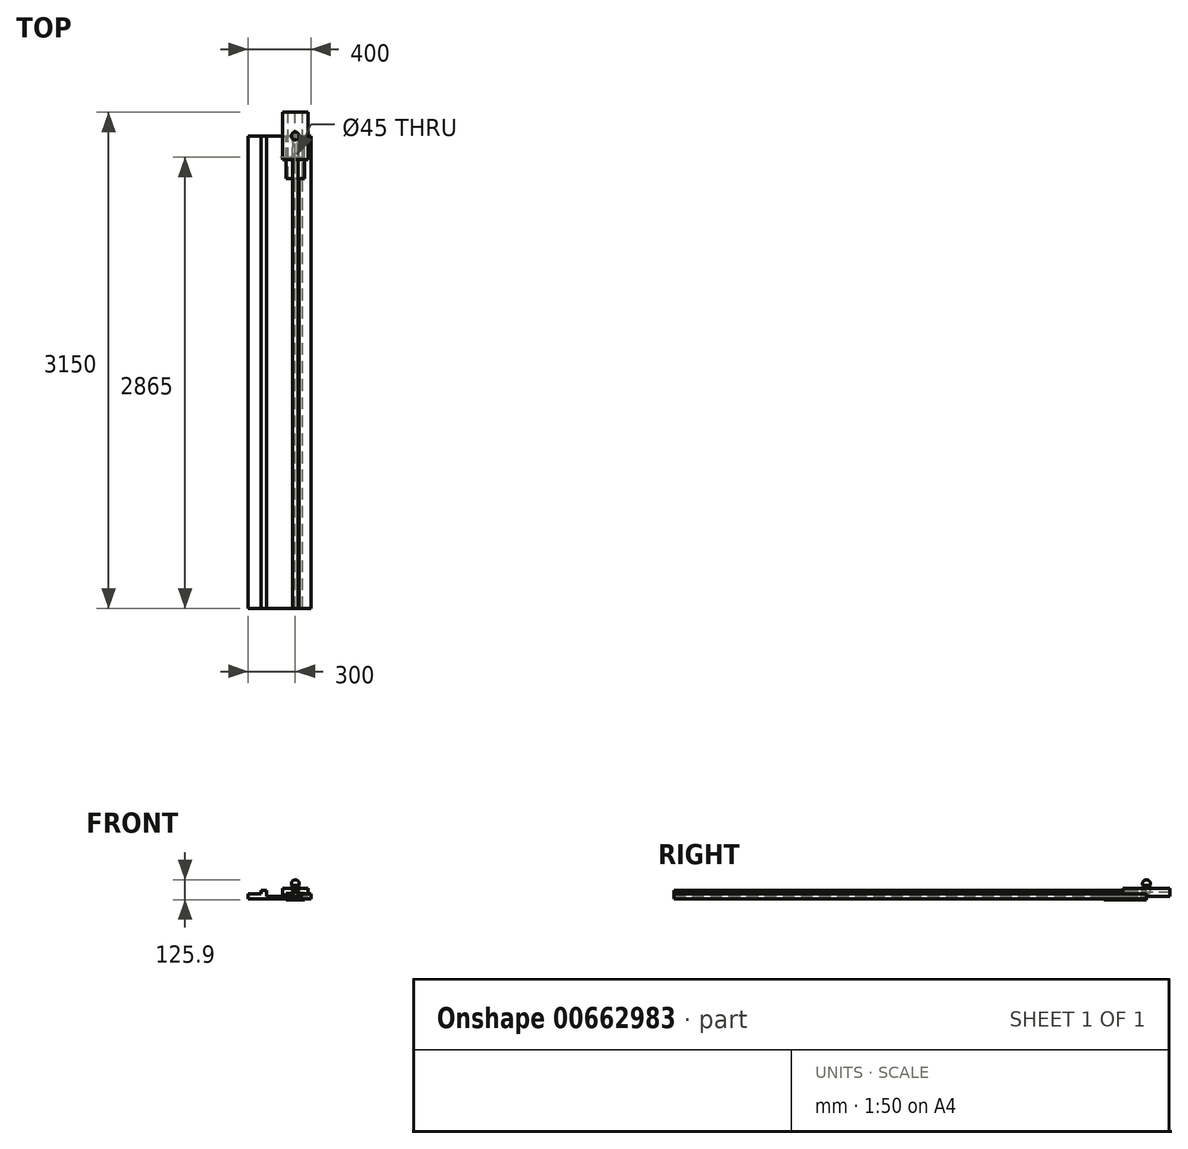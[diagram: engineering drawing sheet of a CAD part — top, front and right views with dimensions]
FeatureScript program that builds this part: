
annotation { "Feature Type Name" : "Feature", "Feature Type Description" : "" }
export const myFeature = defineFeature(function(context is Context, id is Id, definition is map)
    precondition{}
    {
        {
            var Q0;
            Q0=qCreatedBy(makeId("Front.planeOp"),FACE);
            var sketch = newSketch(context, id + "F0", { "sketchPlane" : qUnion([Q0])});
            skLineSegment(sketch, "E0.bottom", {"start": v(100, -15) * mm, "end": v(-100, -15) * mm});
            skLineSegment(sketch, "E0.top", {"start": v(100, 15) * mm, "end": v(-100, 15) * mm});
            skLineSegment(sketch, "E0.left", {"start": v(100, -15) * mm, "end": v(100, 15) * mm});
            skLineSegment(sketch, "E0.right", {"start": v(-100, -15) * mm, "end": v(-100, 15) * mm});
            skPoint(sketch, "E0.middle", {"position": v(0, 0) * mm});
            skLineSegment(sketch, "E1.bottom", {"start": v(-17.5, 15) * mm, "end": v(17.5, 15) * mm});
            skLineSegment(sketch, "E1.top", {"start": v(-17.5, 40) * mm, "end": v(17.5, 40) * mm});
            skLineSegment(sketch, "E1.left", {"start": v(-17.5, 15) * mm, "end": v(-17.5, 40) * mm});
            skLineSegment(sketch, "E1.right", {"start": v(17.5, 15) * mm, "end": v(17.5, 40) * mm});
            skPoint(sketch, "E1.middle", {"position": v(0, 27.5) * mm});
            skLineSegment(sketch, "E2.bottom", {"start": v(-100, 15) * mm, "end": v(-300, 15) * mm});
            skLineSegment(sketch, "E2.top", {"start": v(-100, -15) * mm, "end": v(-300, -15) * mm});
            skLineSegment(sketch, "E2.left", {"start": v(-100, 15) * mm, "end": v(-100, -15) * mm});
            skLineSegment(sketch, "E2.right", {"start": v(-300, 15) * mm, "end": v(-300, -15) * mm});
            skLineSegment(sketch, "E3.bottom", {"start": v(-182.5, 15) * mm, "end": v(-217.5, 15) * mm});
            skLineSegment(sketch, "E3.top", {"start": v(-182.5, 40) * mm, "end": v(-217.5, 40) * mm});
            skLineSegment(sketch, "E3.left", {"start": v(-182.5, 15) * mm, "end": v(-182.5, 40) * mm});
            skLineSegment(sketch, "E3.right", {"start": v(-217.5, 15) * mm, "end": v(-217.5, 40) * mm});
            skPoint(sketch, "E3.middle", {"position": v(-200, 27.5) * mm});
            skPoint(sketch, "E3.middle.positionSnap0", {"position": v(-200, 15) * mm});
            skPoint(sketch, "E3.centerSnap0", {"position": v(-200, 15) * mm});
            skSolve(sketch);
        }
        {
            var Q0;
            Q0=makeQuery(id+"F0.imprint","IMPRINT",FACE,{"disambiguationData":[TD([[makeQuery(id+"F0.imprint","IMPRINT",EDGE,{"derivedFrom":sQuery(id+"F0.wireOp",EDGE,"E1.top")}),-1.0]])]});
            var Q1;
            Q1=makeQuery(id+"F0.imprint","IMPRINT",FACE,{"disambiguationData":[TD([[makeQuery(id+"F0.imprint","IMPRINT",EDGE,{"derivedFrom":sQuery(id+"F0.wireOp",EDGE,"E0.bottom")}),-1.0]])]});
            var Q2;
            Q2=makeQuery(id+"F0.imprint","IMPRINT",FACE,{"disambiguationData":[TD([[makeQuery(id+"F0.imprint","IMPRINT",EDGE,{"derivedFrom":sQuery(id+"F0.wireOp",EDGE,"E3.top")}),1.0]])]});
            var Q3;
            {var subQ3=sQuery(id+"F0.wireOp",EDGE,"E0.right");Q3=makeQuery(id+"F0.imprint","IMPRINT",FACE,{"disambiguationData":[TD([[makeQuery(id+"F0.imprint","IMPRINT",EDGE,{"derivedFrom":subQ3}),1.0]])]});}
            extrude(context, id + "F1", {"entities" : qUnion([Q0, Q1, Q2, Q3]), "depth" : 3000 * mm, "offsetDistance" : 25 * mm});
        }
        {
            var Q0;
            Q0=makeQuery(id+"F1.opExtrude","CAP_FACE",FACE,{"disambiguationData":[OSD([sQuery(id+"F0.wireOp",EDGE,"E0.bottom"),sQuery(id+"F0.wireOp",EDGE,"E0.top"),sQuery(id+"F0.wireOp",EDGE,"E0.left"),sQuery(id+"F0.wireOp",EDGE,"E1.top"),sQuery(id+"F0.wireOp",EDGE,"E1.left"),sQuery(id+"F0.wireOp",EDGE,"E1.right"),sQuery(id+"F0.wireOp",EDGE,"E2.bottom"),sQuery(id+"F0.wireOp",EDGE,"E2.top"),sQuery(id+"F0.wireOp",EDGE,"E2.right"),sQuery(id+"F0.wireOp",EDGE,"E3.top"),sQuery(id+"F0.wireOp",EDGE,"E3.left"),sQuery(id+"F0.wireOp",EDGE,"E3.right")])],"isStart":false});
            var sketch = newSketch(context, id + "F2", { "sketchPlane" : qUnion([Q0])});
            skLineSegment(sketch, "E4.bottom", {"start": v(-182.5, 15) * mm, "end": v(-17.5, 15) * mm});
            skLineSegment(sketch, "E4.top", {"start": v(-182.5, 0) * mm, "end": v(-17.5, 0) * mm});
            skLineSegment(sketch, "E4.left", {"start": v(-182.5, 15) * mm, "end": v(-182.5, 0) * mm});
            skLineSegment(sketch, "E4.right", {"start": v(-17.5, 15) * mm, "end": v(-17.5, 0) * mm});
            skSolve(sketch);
        }
        {
            var Q0;
            Q0=makeQuery(id+"F2.imprint","IMPRINT",FACE,{"disambiguationData":[TD([[makeQuery(id+"F2.imprint","IMPRINT",EDGE,{"derivedFrom":sQuery(id+"F2.wireOp",EDGE,"E4.bottom")}),1.0]])]});
            extrude(context, id + "F3", {"entities" : qUnion([Q0]), "operationType" : NewBodyOperationType.REMOVE, "endBound" : BoundingType.THROUGH_ALL, "oppositeDirection" : true, "depth" : 25 * mm, "offsetDistance" : 25 * mm});
        }
        {
            var Q0;
            Q0=qCreatedBy(makeId("Front.planeOp"),FACE);
            var sketch = newSketch(context, id + "F4", { "sketchPlane" : qUnion([Q0])});
            skLineSegment(sketch, "E5.bottom", {"start": v(57.5, -20) * mm, "end": v(-57.5, -20) * mm});
            skLineSegment(sketch, "E5.top", {"start": v(57.5, 20) * mm, "end": v(-57.5, 20) * mm});
            skLineSegment(sketch, "E5.left", {"start": v(57.5, -20) * mm, "end": v(57.5, 20) * mm});
            skLineSegment(sketch, "E5.right", {"start": v(-57.5, -20) * mm, "end": v(-57.5, 20) * mm});
            skPoint(sketch, "E5.middle", {"position": v(0, 0) * mm});
            skSolve(sketch);
        }
        {
            var Q0;
            Q0=makeQuery(id+"F4.imprint","IMPRINT",FACE,{"disambiguationData":[TD([[makeQuery(id+"F4.imprint","IMPRINT",EDGE,{"derivedFrom":sQuery(id+"F4.wireOp",EDGE,"E5.bottom")}),-1.0]])]});
            extrude(context, id + "F5", {"entities" : qUnion([Q0]), "depth" : 270 * mm, "offsetDistance" : 25 * mm});
        }
        {
            var Q0;
            Q0=makeQuery(id+"F5.opExtrude","SWEPT_FACE",FACE,{"disambiguationData":[OSD([sQuery(id+"F4.wireOp",EDGE,"E5.top")])]});
            var sketch = newSketch(context, id + "F6", { "sketchPlane" : qUnion([Q0])});
            skPoint(sketch, "E6", {"position": v(0, -135) * mm});
            skPoint(sketch, "E6.positionSnap0", {"position": v(-57.5, -135) * mm});
            skSolve(sketch);
        }
        {
            var Q0;
            Q0=sQuery(id+"F6.wireOp",VERTEX,"E6");
            var Q1;
            Q1=makeQuery(id+"F5.opExtrude","SWEPT_BODY",BODY,{"disambiguationData":[OSD([sQuery(id+"F4.wireOp",EDGE,"E5.bottom"),sQuery(id+"F4.wireOp",EDGE,"E5.top"),sQuery(id+"F4.wireOp",EDGE,"E5.left"),sQuery(id+"F4.wireOp",EDGE,"E5.right")])]});
            hole(context, id + "F7", {"style" : HoleStyle.SIMPLE, "endStyle" : HoleEndStyle.THROUGH, "standardTappedOrClearance" : lookupTablePath({ "fit" : "Normal", "standard" : "ISO", "size" : "M42", "type" : "Clearance" }), "standardBlindInLast" : lookupTablePath({ "fit" : "Normal", "standard" : "ISO", "engagement" : "75%", "pitch" : "3 mm", "size" : "M42", "type" : "Clearance & tapped" }), "holeDiameter" : 45 * mm, "majorDiameter" : 5 * mm, "isTappedThrough" : true, "tappedDepth" : 16 * mm, "tapClearance" : 3, "locations" : qUnion([Q0]), "scope" : qUnion([Q1])});
        }
        {
            var Q0;
            Q0=qCreatedBy(makeId("Right.planeOp"),FACE);
            var sketch = newSketch(context, id + "F8", { "sketchPlane" : qUnion([Q0])});
            skLineSegment(sketch, "E7", {"start": v(-22.5, 0) * mm, "end": v(-22.5, 70) * mm});
            skLineSegment(sketch, "E8", {"start": v(-22.5, 0) * mm, "end": v(0, 0) * mm});
            skLineSegment(sketch, "E9", {"start": v(0, 0) * mm, "end": v(0, 80.9) * mm});
            skArc(sketch, "E10", {"start": v(-22.5, 70) * mm, "mid": v(-21.18, 94.17) * mm, "end": v(0, 105.9) * mm});
            skLineSegment(sketch, "E11", {"start": v(0, 80.9) * mm, "end": v(0, 105.9) * mm});
            skLineSegment(sketch, "E12", {"start": v(-22.5, 70) * mm, "end": v(-17.5, 70) * mm});
            skLineSegment(sketch, "E13", {"start": v(-17.5, 70) * mm, "end": v(-17.5, 65) * mm});
            skLineSegment(sketch, "E14", {"start": v(-17.5, 65) * mm, "end": v(-22.5, 65) * mm});
            skSolve(sketch);
        }
        {
            var Q0;
            {var subQ0=sQuery(id+"F8.wireOp",EDGE,"E8");Q0=makeQuery(id+"F8.imprint","IMPRINT",FACE,{"disambiguationData":[TD([[makeQuery(id+"F8.imprint","IMPRINT",EDGE,{"derivedFrom":subQ0}),1.0]])]});}
            var Q1;
            Q1=sQuery(id+"F8.wireOp",EDGE,"E9");
            revolve(context, id + "F9", {"surfaceOperationType" : NewSurfaceOperationType.NEW, "entities" : qUnion([Q0]), "axis" : qUnion([Q1]), "revolveType" : RevolveType.FULL});
        }
        {
            var Q0;
            Q0=qCreatedBy(makeId("Front.planeOp"),FACE);
            var sketch = newSketch(context, id + "F10", { "sketchPlane" : qUnion([Q0])});
            skLineSegment(sketch, "E15.bottom", {"start": v(80, 0) * mm, "end": v(-80, 0) * mm});
            skLineSegment(sketch, "E15.top", {"start": v(80, 50) * mm, "end": v(-80, 50) * mm});
            skLineSegment(sketch, "E15.left", {"start": v(80, 0) * mm, "end": v(80, 50) * mm});
            skLineSegment(sketch, "E15.right", {"start": v(-80, 0) * mm, "end": v(-80, 50) * mm});
            skPoint(sketch, "E15.middle", {"position": v(0, 25) * mm});
            skSolve(sketch);
        }
        {
            var Q0;
            Q0=makeQuery(id+"F10.imprint","IMPRINT",FACE,{"disambiguationData":[TD([[makeQuery(id+"F10.imprint","IMPRINT",EDGE,{"derivedFrom":sQuery(id+"F10.wireOp",EDGE,"E15.bottom")}),-1.0]])]});
            extrude(context, id + "F11", {"entities" : qUnion([Q0]), "depth" : 150 * mm, "offsetDistance" : 25 * mm, "hasSecondDirection" : true, "secondDirectionOppositeDirection" : true, "secondDirectionDepth" : 150 * mm});
        }
        {
            var Q0;
            Q0=qCreatedBy(makeId("Front.planeOp"),FACE);
            var sketch = newSketch(context, id + "F12", { "sketchPlane" : qUnion([Q0])});
            skLineSegment(sketch, "E16", {"start": v(25, 0) * mm, "end": v(0, 0) * mm});
            skArc(sketch, "E17", {"start": v(25, 0) * mm, "mid": v(17.68, 17.68) * mm, "end": v(0, 25) * mm});
            skLineSegment(sketch, "E18", {"start": v(0, 25) * mm, "end": v(0, 0) * mm});
            skSolve(sketch);
        }
        {
            var Q0;
            Q0=makeQuery(id+"F12.imprint","IMPRINT",FACE,{"disambiguationData":[TD([[makeQuery(id+"F12.imprint","IMPRINT",EDGE,{"derivedFrom":sQuery(id+"F12.wireOp",EDGE,"E16")}),-1.0]])]});
            var Q1;
            Q1=sQuery(id+"F12.wireOp",EDGE,"E18");
            revolve(context, id + "F13", {"surfaceOperationType" : NewSurfaceOperationType.NEW, "entities" : qUnion([Q0]), "axis" : qUnion([Q1]), "revolveType" : RevolveType.FULL});
        }
        {
            var Q0;
            Q0=makeQuery(id+"F13.opRevolve","SWEPT_BODY",BODY,{"disambiguationData":[OSD([sQuery(id+"F12.wireOp",EDGE,"E16"),sQuery(id+"F12.wireOp",EDGE,"E17"),sQuery(id+"F12.wireOp",EDGE,"E18")])]});
            var Q1;
            Q1=makeQuery(id+"F11.opExtrude","SWEPT_BODY",BODY,{"disambiguationData":[OSD([sQuery(id+"F10.wireOp",EDGE,"E15.bottom"),sQuery(id+"F10.wireOp",EDGE,"E15.top"),sQuery(id+"F10.wireOp",EDGE,"E15.left"),sQuery(id+"F10.wireOp",EDGE,"E15.right")])]});
            booleanBodies(context, id + "F14", {"operationType" : BooleanOperationType.SUBTRACTION, "tools" : qUnion([Q0]), "targets" : qUnion([Q1])});
        }
        {
            var Q0;
            Q0=makeQuery(id+"F10.imprint","IMPRINT",FACE,{"disambiguationData":[TD([[makeQuery(id+"F10.imprint","IMPRINT",EDGE,{"derivedFrom":sQuery(id+"F10.wireOp",EDGE,"E15.bottom")}),-1.0]])]});
            extrude(context, id + "F15", {"entities" : qUnion([Q0]), "depth" : 150 * mm, "offsetDistance" : 25 * mm, "hasSecondDirection" : true, "secondDirectionOppositeDirection" : true, "secondDirectionDepth" : 150 * mm});
        }
        {
            var Q0;
            Q0=makeQuery(id+"F15.opExtrude","CAP_FACE",FACE,{"disambiguationData":[OSD([sQuery(id+"F10.wireOp",EDGE,"E15.bottom"),sQuery(id+"F10.wireOp",EDGE,"E15.top"),sQuery(id+"F10.wireOp",EDGE,"E15.left"),sQuery(id+"F10.wireOp",EDGE,"E15.right")])],"isStart":true});
            var sketch = newSketch(context, id + "F16", { "sketchPlane" : qUnion([Q0])});
            skLineSegment(sketch, "E19", {"start": v(-45.23, 0) * mm, "end": v(0, 30) * mm});
            skPoint(sketch, "E19.endSnap0", {"position": v(0, 0) * mm});
            skLineSegment(sketch, "E20", {"start": v(0, 30) * mm, "end": v(45.23, 0) * mm});
            skArc(sketch, "E21", {"start": v(-25, 0) * mm, "mid": v(0, 25) * mm, "end": v(25, 0) * mm, "construction": true});
            skSolve(sketch);
        }
        {
            var Q0;
            {var subQ0=sQuery(id+"F16.wireOp",EDGE,"E19");Q0=makeQuery(id+"F16.imprint","IMPRINT",FACE,{"disambiguationData":[TD([[makeQuery(id+"F16.imprint","IMPRINT",EDGE,{"derivedFrom":subQ0}),-1.0]])]});}
            extrude(context, id + "F17", {"entities" : qUnion([Q0]), "operationType" : NewBodyOperationType.REMOVE, "endBound" : BoundingType.THROUGH_ALL, "oppositeDirection" : true, "depth" : 25 * mm, "offsetDistance" : 25 * mm});
        }
    });
